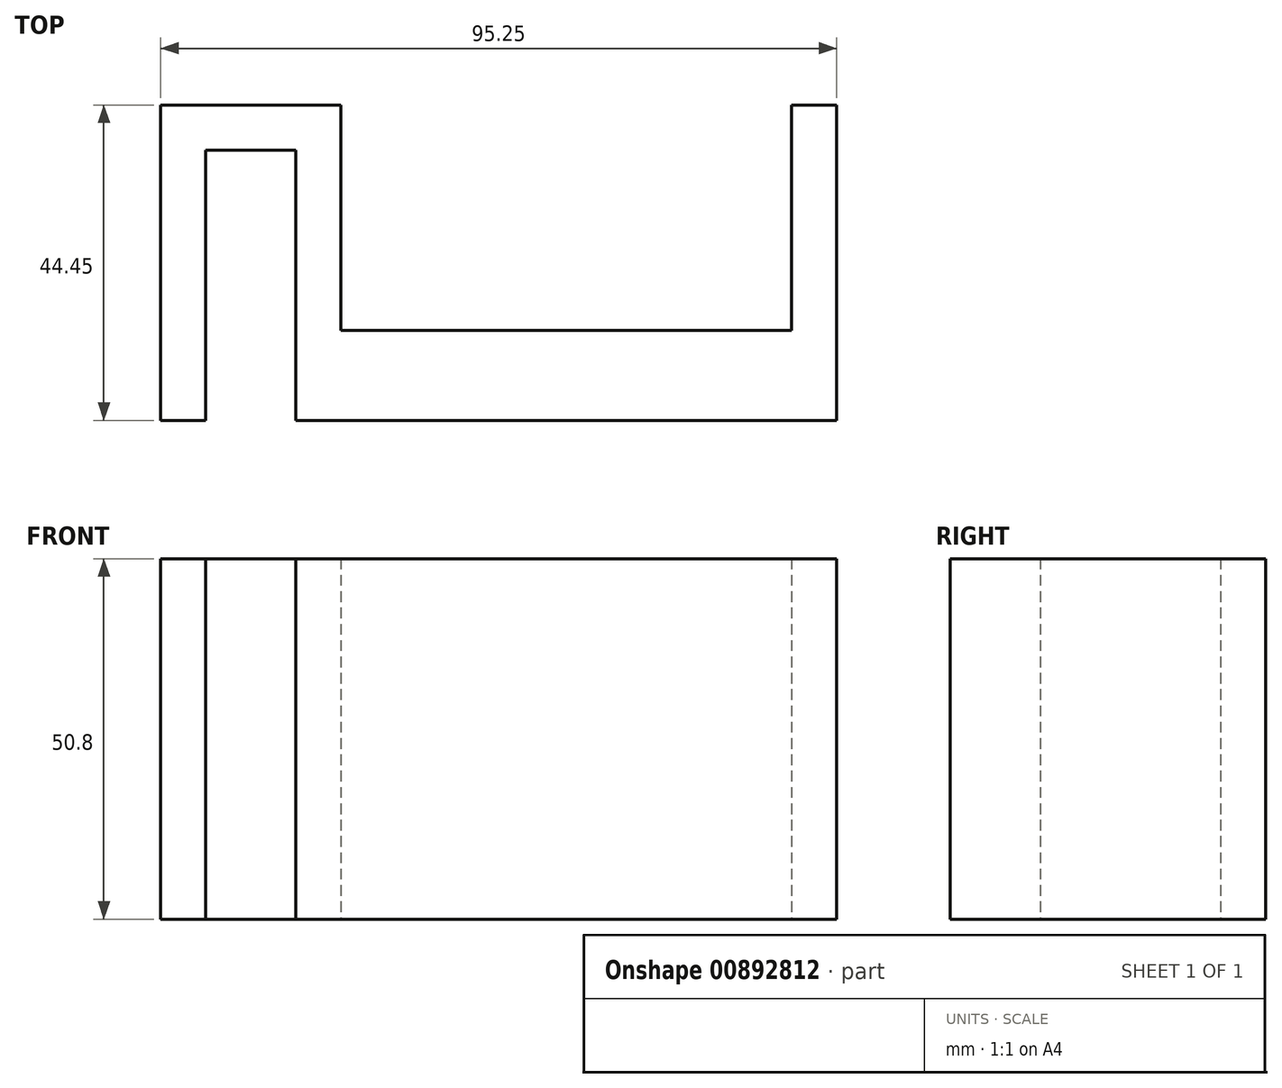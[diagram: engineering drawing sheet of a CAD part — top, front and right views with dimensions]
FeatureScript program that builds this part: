
annotation { "Feature Type Name" : "Feature", "Feature Type Description" : "" }
export const myFeature = defineFeature(function(context is Context, id is Id, definition is map)
    precondition{}
    {
        {
            var Q0;
            Q0=qCreatedBy(makeId("Top.planeOp"),FACE);
            var sketch = newSketch(context, id + "F0", { "sketchPlane" : qUnion([Q0])});
            skLineSegment(sketch, "E0", {"start": v(-19.05, 0) * mm, "end": v(-19.05, 44.45) * mm});
            skLineSegment(sketch, "E1", {"start": v(-19.05, 44.45) * mm, "end": v(6.35, 44.45) * mm});
            skLineSegment(sketch, "E2", {"start": v(6.35, 44.45) * mm, "end": v(6.35, 12.7) * mm});
            skLineSegment(sketch, "E3", {"start": v(6.35, 12.7) * mm, "end": v(69.85, 12.7) * mm});
            skLineSegment(sketch, "E4", {"start": v(69.85, 12.7) * mm, "end": v(69.85, 44.45) * mm});
            skLineSegment(sketch, "E5", {"start": v(69.85, 44.45) * mm, "end": v(76.2, 44.45) * mm});
            skLineSegment(sketch, "E6", {"start": v(76.2, 44.45) * mm, "end": v(76.2, 0) * mm});
            skLineSegment(sketch, "E7", {"start": v(76.2, 0) * mm, "end": v(0, 0) * mm});
            skLineSegment(sketch, "E8", {"start": v(0, 0) * mm, "end": v(0, 38.1) * mm});
            skLineSegment(sketch, "E9", {"start": v(0, 38.1) * mm, "end": v(-12.7, 38.1) * mm});
            skLineSegment(sketch, "E10", {"start": v(-12.7, 38.1) * mm, "end": v(-12.7, 0) * mm});
            skLineSegment(sketch, "E11", {"start": v(-12.7, 0) * mm, "end": v(-19.05, 0) * mm});
            skSolve(sketch);
        }
        {
            var Q0;
            Q0 = qSketchRegion(id + "F0", true);
            extrude(context, id + "F1", {"entities" : qUnion([Q0]), "depth" : 50.8 * mm, "offsetDistance" : 25 * mm});
        }
    });
